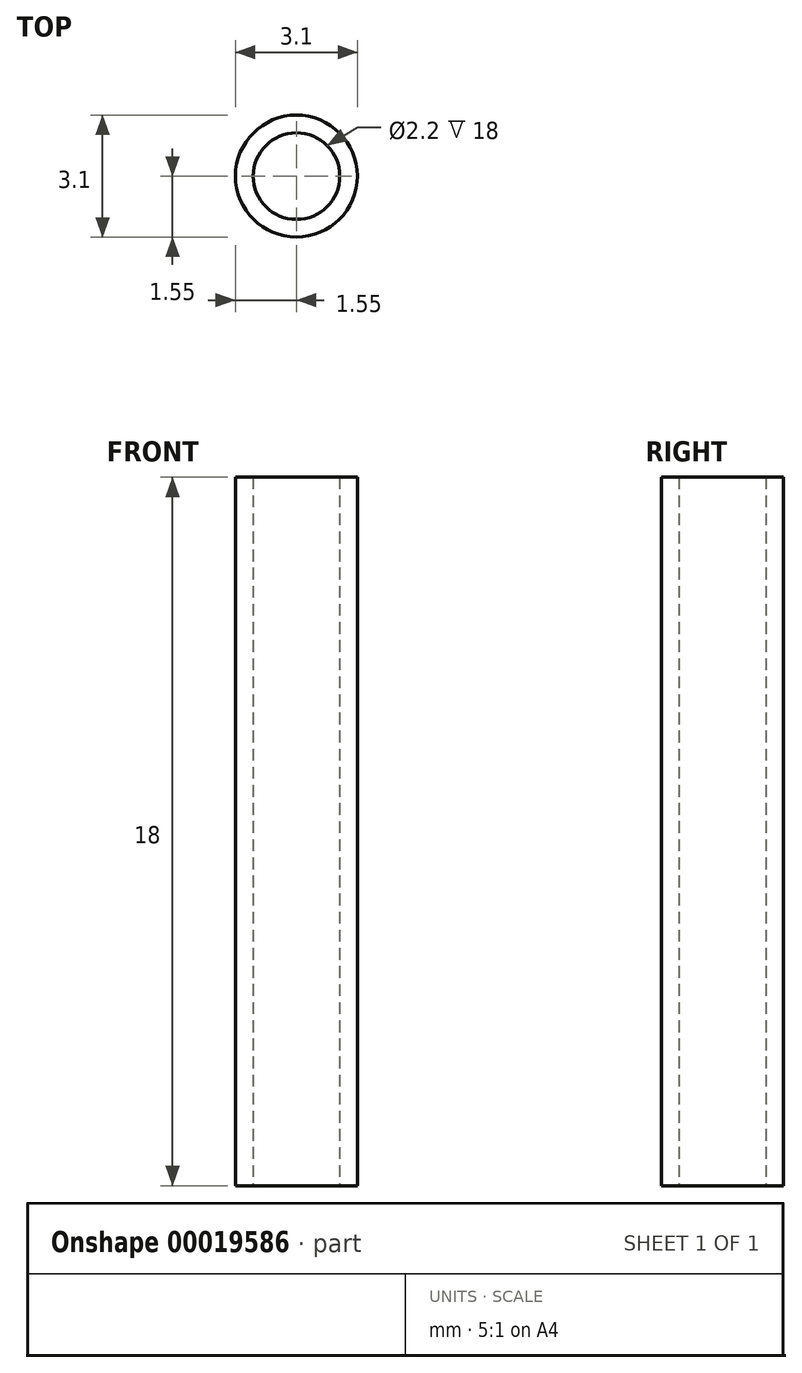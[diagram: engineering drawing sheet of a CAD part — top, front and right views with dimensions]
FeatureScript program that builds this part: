
annotation { "Feature Type Name" : "Feature", "Feature Type Description" : "" }
export const myFeature = defineFeature(function(context is Context, id is Id, definition is map)
    precondition{}
    {
        {
            var Q0;
            Q0=qCreatedBy(makeId("Top.planeOp"),FACE);
            var sketch = newSketch(context, id + "F0", { "sketchPlane" : qUnion([Q0])});
            skCircle(sketch, "E0", {"center": v(0, 0) * mm, "radius": 1.55 * mm});
            skCircle(sketch, "E1", {"center": v(0, 0) * mm, "radius": 1.1 * mm});
            skSolve(sketch);
        }
        {
            var Q0;
            Q0 = qSketchRegion(id + "F0", true);
            extrude(context, id + "F1", {"entities" : qUnion([Q0]), "depth" : 18 * mm});
        }
    });
